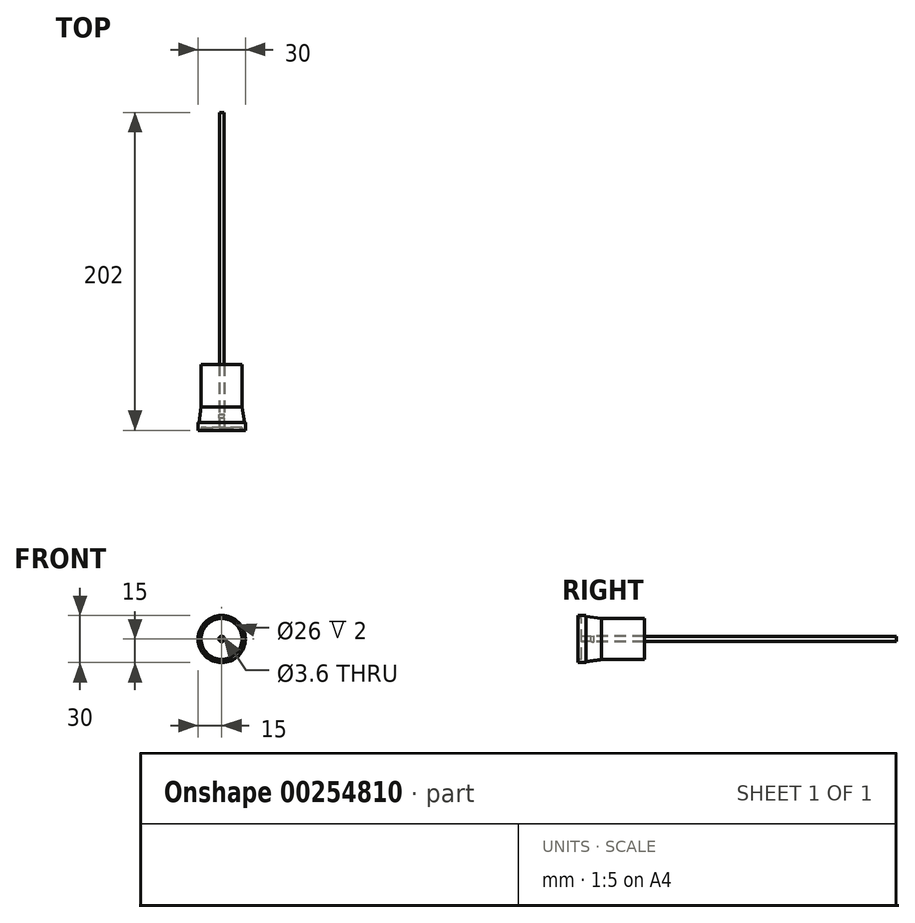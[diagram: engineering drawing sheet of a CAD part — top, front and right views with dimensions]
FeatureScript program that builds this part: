
annotation { "Feature Type Name" : "Feature", "Feature Type Description" : "" }
export const myFeature = defineFeature(function(context is Context, id is Id, definition is map)
    precondition{}
    {
        {
            var Q0;
            Q0=qCreatedBy(makeId("Front.planeOp"),FACE);
            var sketch = newSketch(context, id + "F0", { "sketchPlane" : qUnion([Q0])});
            skCircle(sketch, "E0", {"center": v(0, 0) * mm, "radius": 1.56 * mm});
            skCircle(sketch, "E1", {"center": v(0, 0) * mm, "radius": 15 * mm});
            skCircle(sketch, "E2", {"center": v(0, 0) * mm, "radius": 12.5 * mm});
            skSolve(sketch);
        }
        {
            var Q0;
            Q0=qCreatedBy(makeId("Right.planeOp"),FACE);
            var sketch = newSketch(context, id + "F1", { "sketchPlane" : qUnion([Q0])});
            skLineSegment(sketch, "E3.0", {"start": v(0, -15) * mm, "end": v(0, 15) * mm});
            skLineSegment(sketch, "E4", {"start": v(0, 15) * mm, "end": v(40, 15) * mm});
            skLineSegment(sketch, "E5", {"start": v(0, 15) * mm, "end": v(-2, 15) * mm});
            skLineSegment(sketch, "E6", {"start": v(40, 15) * mm, "end": v(40, 0) * mm});
            skLineSegment(sketch, "E7", {"start": v(0, 1.8) * mm, "end": v(6, 1.8) * mm, "construction": true});
            skLineSegment(sketch, "E8", {"start": v(0, 1.8) * mm, "end": v(6, 1.65) * mm});
            skLineSegment(sketch, "E9", {"start": v(6, 1.65) * mm, "end": v(6, 0) * mm});
            skLineSegment(sketch, "E10", {"start": v(6, 0) * mm, "end": v(40, 0) * mm});
            skLineSegment(sketch, "E11", {"start": v(-2, 15) * mm, "end": v(-2, 13) * mm});
            skLineSegment(sketch, "E12", {"start": v(-2, 13) * mm, "end": v(0, 13) * mm});
            skLineSegment(sketch, "E13", {"start": v(6, 1.65) * mm, "end": v(8.19, 1.8) * mm});
            skLineSegment(sketch, "E14", {"start": v(8.19, 1.8) * mm, "end": v(40, 1.8) * mm});
            skLineSegment(sketch, "E15", {"start": v(3.04, 15) * mm, "end": v(3.04, 14.42) * mm});
            skLineSegment(sketch, "E16", {"start": v(12.92, 13.05) * mm, "end": v(40, 13.05) * mm});
            skLineSegment(sketch, "E17", {"start": v(3.04, 14.42) * mm, "end": v(12.92, 13.05) * mm});
            skSolve(sketch);
        }
        {
            var Q0;
            {var subQ0=sQuery(id+"F1.wireOp",EDGE,"E5");Q0=makeQuery(id+"F1.imprint","IMPRINT",FACE,{"disambiguationData":[TD([[makeQuery(id+"F1.imprint","IMPRINT",EDGE,{"derivedFrom":subQ0}),1.0]])]});}
            var Q1;
            {var subQ7=sQuery(id+"F1.wireOp",EDGE,"E8");Q1=makeQuery(id+"F1.imprint","IMPRINT",FACE,{"disambiguationData":[TD([[makeQuery(id+"F1.imprint","IMPRINT",EDGE,{"derivedFrom":subQ7}),1.0]])]});}
            var Q2;
            Q2=sQuery(id+"F1.wireOp",EDGE,"E10");
            revolve(context, id + "F2", {"entities" : qUnion([Q0, Q1]), "axis" : qUnion([Q2]), "revolveType" : RevolveType.FULL});
        }
        {
            var Q0;
            Q0=qCreatedBy(makeId("Front.planeOp"),FACE);
            var sketch = newSketch(context, id + "F3", { "sketchPlane" : qUnion([Q0])});
            skCircle(sketch, "E18", {"center": v(0, 0) * mm, "radius": 1.5 * mm});
            skSolve(sketch);
        }
        {
            var Q0;
            Q0=makeQuery(id+"F3.imprint","IMPRINT",FACE,{"disambiguationData":[TD([[makeQuery(id+"F3.imprint","IMPRINT",EDGE,{"derivedFrom":sQuery(id+"F3.wireOp",EDGE,"E18")}),1.0]])]});
            extrude(context, id + "F4", {"entities" : qUnion([Q0]), "oppositeDirection" : true, "depth" : 200 * mm});
        }
    });
